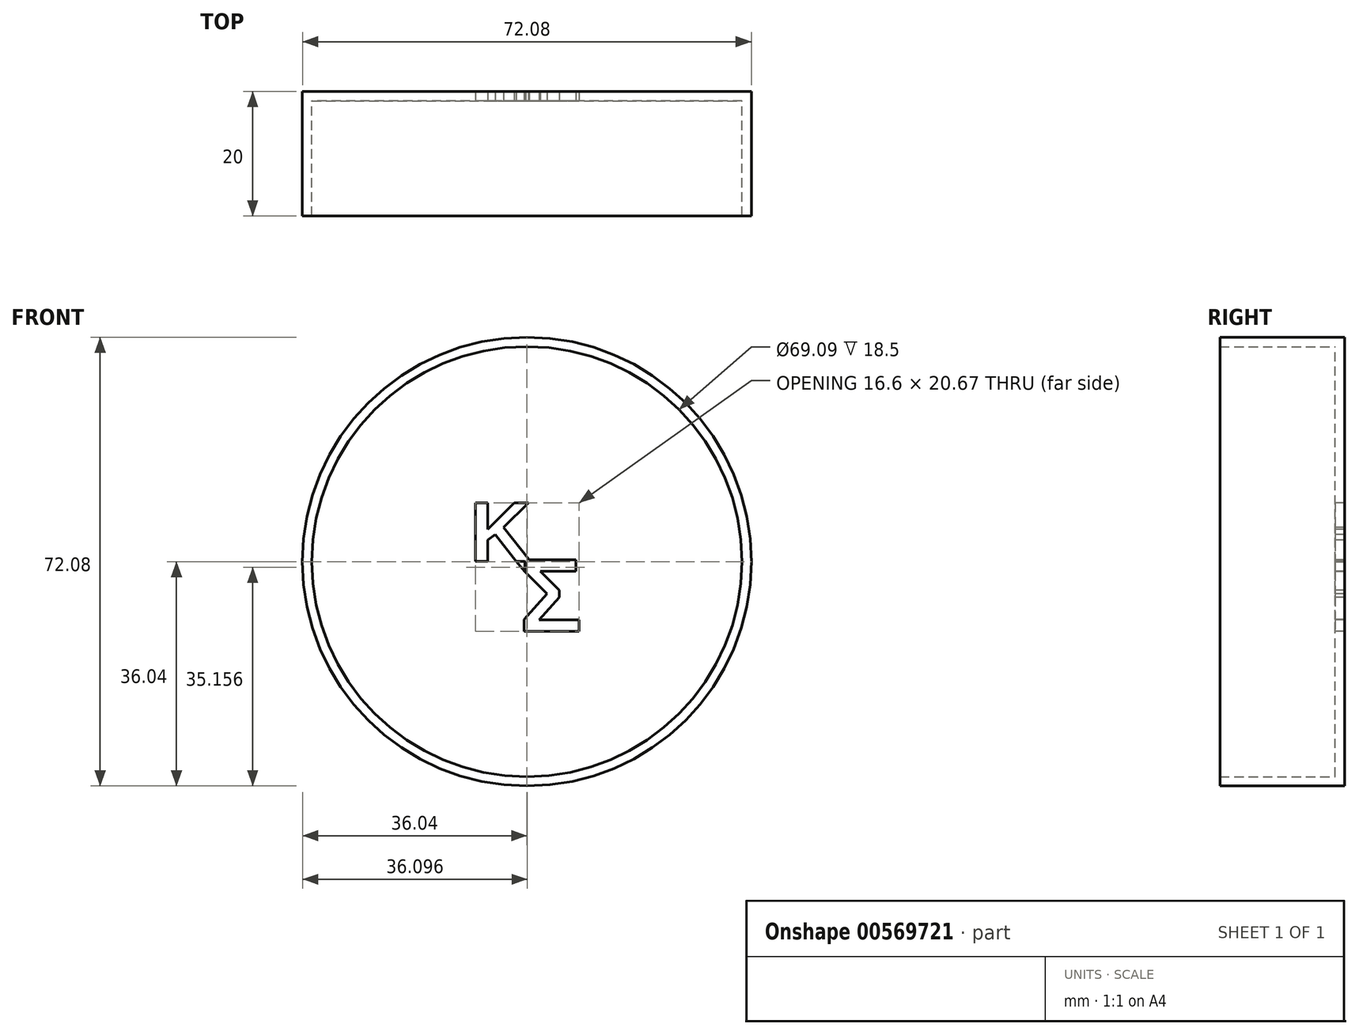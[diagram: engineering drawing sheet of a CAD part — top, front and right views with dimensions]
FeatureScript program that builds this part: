
annotation { "Feature Type Name" : "Feature", "Feature Type Description" : "" }
export const myFeature = defineFeature(function(context is Context, id is Id, definition is map)
    precondition{}
    {
        {
            var Q0;
            Q0=qCreatedBy(makeId("Front.planeOp"),FACE);
            var sketch = newSketch(context, id + "F0", { "sketchPlane" : qUnion([Q0])});
            skCircle(sketch, "E0", {"center": v(0, 0) * mm, "radius": 36.04 * mm});
            skSolve(sketch);
        }
        {
            var Q0;
            Q0=makeQuery(id+"F0.imprint","IMPRINT",FACE,{"disambiguationData":[TD([[makeQuery(id+"F0.imprint","IMPRINT",EDGE,{"derivedFrom":sQuery(id+"F0.wireOp",EDGE,"E0")}),1.0]])]});
            extrude(context, id + "F1", {"entities" : qUnion([Q0]), "depth" : 20 * mm, "offsetDistance" : 25 * mm});
        }
        {
            var Q0;
            Q0=makeQuery(id+"F1.opExtrude","CAP_FACE",FACE,{"disambiguationData":[OSD([sQuery(id+"F0.wireOp",EDGE,"E0")])],"isStart":false});
            shell(context, id + "F2", {"entities" : qUnion([Q0]), "thickness" : 1.5 * mm});
        }
        {
            var Q0;
            {var subQ0=sQuery(id+"F0.wireOp",EDGE,"E0");Q0=makeQuery(id+"F2.opShell","OFFSET_FACE",FACE,{"disambiguationData":[OSD([subQ0]),TDD([makeQuery(id+"F1.opExtrude","CAP_FACE",FACE,{"disambiguationData":[OSD([subQ0])],"isStart":true})])]});}
            var sketch = newSketch(context, id + "F3", { "sketchPlane" : qUnion([Q0])});
            skCircle(sketch, "E1", {"center": v(0, 0) * mm, "radius": 14 * mm});
            skSolve(sketch);
        }
        {
            var Q0;
            Q0=makeQuery(id+"F3.imprint","IMPRINT",FACE,{"disambiguationData":[TD([[makeQuery(id+"F3.imprint","IMPRINT",EDGE,{"derivedFrom":sQuery(id+"F3.wireOp",EDGE,"E1")}),1.0]])]});
            var sketch = newSketch(context, id + "F4", { "sketchPlane" : qUnion([Q0])});
            skText(sketch, "E2", { "text": "K", "fontName": "Arimo-Bold.ttf"});
            skText(sketch, "E3", { "text": "Σ", "fontName": "Arimo-Bold.ttf"});
            skLineSegment(sketch, "E4", {"start": v(-1.74, 0.04) * mm, "end": v(-1.18, 0.04) * mm});
            skLineSegment(sketch, "E5", {"start": v(-1.18, 0.04) * mm, "end": v(-1.18, -0.6) * mm});
            skLineSegment(sketch, "E6", {"start": v(-0.3, -1.6) * mm, "end": v(-0.3, 0.04) * mm});
            skLineSegment(sketch, "E7", {"start": v(-0.3, 0.04) * mm, "end": v(-1.74, 0.04) * mm});
            skLineSegment(sketch, "E8", {"start": v(-1.74, 0.04) * mm, "end": v(-0.3, -1.6) * mm});
            skLineSegment(sketch, "E9", {"start": v(-1.74, 0.04) * mm, "end": v(-0.3, 0.1) * mm});
            skLineSegment(sketch, "E10", {"start": v(-0.3, 0.1) * mm, "end": v(-0.22, 0) * mm});
            skLineSegment(sketch, "E11", {"start": v(-0.22, 0) * mm, "end": v(-0.3, -1.6) * mm});
            skLineSegment(sketch, "E12", {"start": v(-0.27, 0.1) * mm, "end": v(-0.34, 0.1) * mm});
            skLineSegment(sketch, "E13", {"start": v(-0.34, 0.1) * mm, "end": v(-0.33, 0.02) * mm});
            skLineSegment(sketch, "E14", {"start": v(-0.33, 0.02) * mm, "end": v(-0.23, 0.02) * mm});
            skLineSegment(sketch, "E15", {"start": v(-0.23, 0.02) * mm, "end": v(-0.27, 0.1) * mm});
            const initialGuessF4  = {"E2": [-0.00916, 4e-05, 1, 0, 0.00985], "E3": [-0.00118, -0.01122, 1, 0, 0.01205]};
            skSetInitialGuess(sketch, initialGuessF4);
            skSolve(sketch);
        }
        {
            var Q0;
            Q0 = qSketchRegion(id + "F4", true);
            extrude(context, id + "F5", {"entities" : qUnion([Q0]), "operationType" : NewBodyOperationType.REMOVE, "oppositeDirection" : true, "depth" : 2 * mm, "offsetDistance" : 25 * mm});
        }
        {
            var Q0;
            Q0=makeQuery(id+"F3.imprint","IMPRINT",FACE,{"disambiguationData":[TD([[makeQuery(id+"F3.imprint","IMPRINT",EDGE,{"derivedFrom":sQuery(id+"F3.wireOp",EDGE,"E1")}),1.0]])]});
            var sketch = newSketch(context, id + "F6", { "sketchPlane" : qUnion([Q0])});
            skLineSegment(sketch, "E16", {"start": v(-0.28, 0.14) * mm, "end": v(-0.38, 0.12) * mm});
            skLineSegment(sketch, "E17", {"start": v(-0.38, 0.12) * mm, "end": v(-0.37, 0) * mm});
            skLineSegment(sketch, "E18", {"start": v(-0.37, 0) * mm, "end": v(-0.2, 0) * mm});
            skLineSegment(sketch, "E19", {"start": v(-0.2, 0) * mm, "end": v(-0.22, 0.12) * mm});
            skLineSegment(sketch, "E20", {"start": v(-0.22, 0.12) * mm, "end": v(-0.28, 0.14) * mm});
            skSolve(sketch);
        }
        {
            var Q0;
            Q0 = qSketchRegion(id + "F6", true);
            extrude(context, id + "F7", {"entities" : qUnion([Q0]), "operationType" : NewBodyOperationType.REMOVE, "oppositeDirection" : true, "depth" : 2 * mm, "offsetDistance" : 25 * mm});
        }
    });
